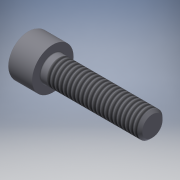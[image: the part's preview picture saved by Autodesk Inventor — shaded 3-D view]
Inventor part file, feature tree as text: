
AUTODESK INVENTOR PART (.ipt)
format: ipt  version: 2017.1 (Build 211199000, 199)  size: 193,024 bytes
history: native  units: mm (DEFAULTED — no unit token found)
features: sketch x2, extrude x1, plane x1, fillet x1
ambient origin geometry x7: Origin, YZ Plane, XY Plane, X Axis, Y Axis, Z Axis, Center Point
bodies: Solid1 (feature_tree), Body (feature_tree)
feature tree (5):
  extrude  "Slot"  Depth=4.826mm
  plane  "Work Plane1"
  fillet  "Fillet2"  Radius=4.826mm
  sketch  "Sketch1"  dims[d1=17.859048mm d2=1.190852mm d3=4.826mm]
  sketch  "Sketch2"  dims[d4=2.286mm d5=60.0deg d6=4.826mm d7=4.826mm d8=4.575385mm d9=7.9248mm d10=90.0deg d11=10.0mm d12=0.0mm d13=17.859048mm d14=0.0mm d15=0.47244mm d16=0.47244mm d17=0.4572mm d19=0.0mm d26=19.05mm d27=45.0deg d28=0.0mm d29=0.0mm d30=0.1524mm]
